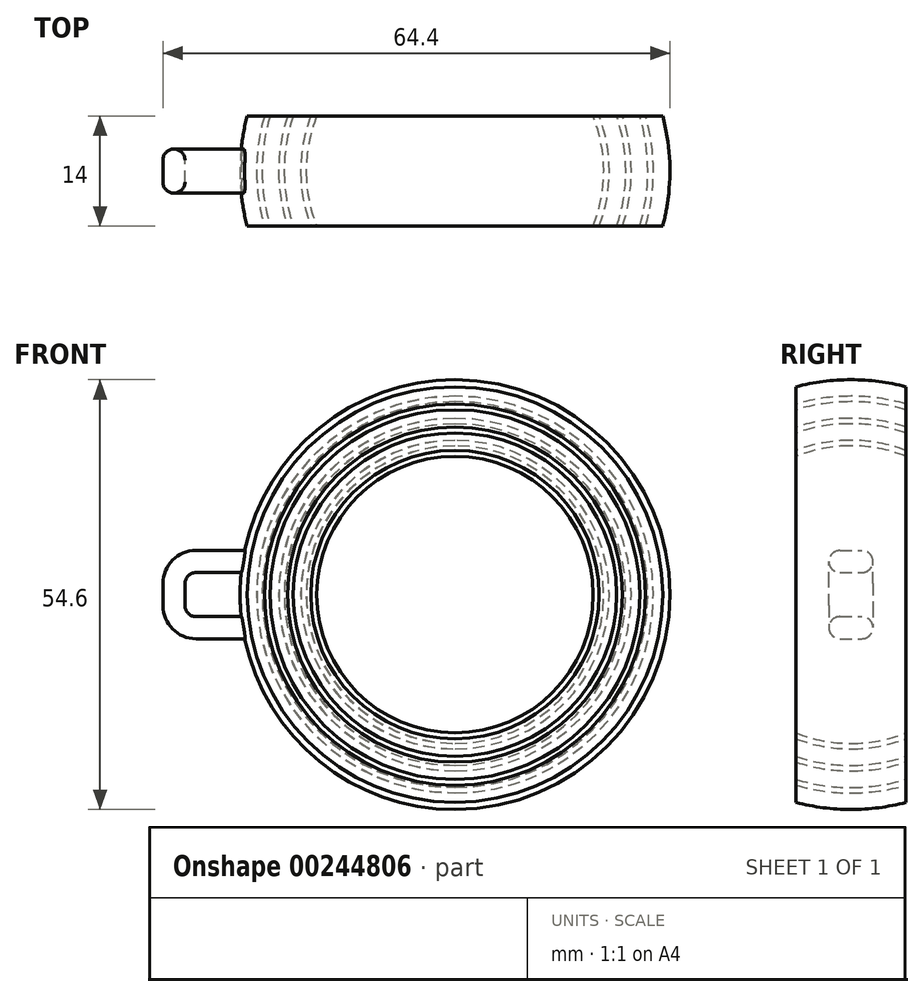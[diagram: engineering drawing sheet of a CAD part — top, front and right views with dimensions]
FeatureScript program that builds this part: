
annotation { "Feature Type Name" : "Feature", "Feature Type Description" : "" }
export const myFeature = defineFeature(function(context is Context, id is Id, definition is map)
    precondition{}
    {
        {
            var Q0;
            Q0=qCreatedBy(makeId("Front.planeOp"),FACE);
            var sketch = newSketch(context, id + "F0", { "sketchPlane" : qUnion([Q0])});
            skCircle(sketch, "E0", {"center": v(0, 0) * mm, "radius": 13.5 * mm});
            skCircle(sketch, "E1.0", {"center": v(0, 0) * mm, "radius": 14 * mm});
            skCircle(sketch, "E2.0", {"center": v(0, 0) * mm, "radius": 15.5 * mm});
            skCircle(sketch, "E3.0", {"center": v(0, 0) * mm, "radius": 16 * mm});
            skCircle(sketch, "E4.0", {"center": v(0, 0) * mm, "radius": 17.5 * mm});
            skCircle(sketch, "E5.0", {"center": v(0, 0) * mm, "radius": 18 * mm});
            skCircle(sketch, "E6.0", {"center": v(0, 0) * mm, "radius": 19.5 * mm});
            skLineSegment(sketch, "E7", {"start": v(0, 19.5) * mm, "end": v(0, -19.5) * mm});
            skSolve(sketch);
        }
        {
            var Q0;
            Q0=qCreatedBy(makeId("Top.planeOp"),FACE);
            var sketch = newSketch(context, id + "F1", { "sketchPlane" : qUnion([Q0])});
            skCircle(sketch, "E8", {"center": v(0, 0) * mm, "radius": 15 * mm});
            skSolve(sketch);
        }
        {
            var Q0;
            {var subQ0=sQuery(id+"F0.wireOp",EDGE,"E7");var subQ1=sQuery(id+"F0.wireOp",EDGE,"E0");var subQ2=makeQuery(id+"F0.imprint","INTERSECT",VERTEX,{"disambiguationData":[OD(0.0)],"derivedFrom":[subQ1,subQ0]});Q0=makeQuery(id+"F0.imprint","IMPRINT",FACE,{"disambiguationData":[TD([[makeQuery(id+"F0.imprint","IMPRINT",EDGE,{"disambiguationData":[TD([[subQ2,1.0]])],"derivedFrom":subQ1}),1.0]])]});}
            var Q1;
            {var subQ0=sQuery(id+"F0.wireOp",EDGE,"E7");var subQ1=sQuery(id+"F0.wireOp",EDGE,"E1.0");var subQ2=makeQuery(id+"F0.imprint","INTERSECT",VERTEX,{"disambiguationData":[OD(0.0)],"derivedFrom":[subQ1,subQ0]});Q1=makeQuery(id+"F0.imprint","IMPRINT",FACE,{"disambiguationData":[TD([[makeQuery(id+"F0.imprint","IMPRINT",EDGE,{"disambiguationData":[TD([[subQ2,1.0]])],"derivedFrom":subQ1}),-1.0]])]});}
            var Q2;
            {var subQ0=sQuery(id+"F0.wireOp",EDGE,"E7");var subQ1=sQuery(id+"F0.wireOp",EDGE,"E3.0");var subQ2=makeQuery(id+"F0.imprint","INTERSECT",VERTEX,{"disambiguationData":[OD(0.0)],"derivedFrom":[subQ1,subQ0]});Q2=makeQuery(id+"F0.imprint","IMPRINT",FACE,{"disambiguationData":[TD([[makeQuery(id+"F0.imprint","IMPRINT",EDGE,{"disambiguationData":[TD([[subQ2,1.0]])],"derivedFrom":subQ1}),-1.0]])]});}
            var Q3;
            {var subQ0=sQuery(id+"F0.wireOp",EDGE,"E7");var subQ1=sQuery(id+"F0.wireOp",EDGE,"E5.0");var subQ2=makeQuery(id+"F0.imprint","INTERSECT",VERTEX,{"disambiguationData":[OD(0.0)],"derivedFrom":[subQ1,subQ0]});Q3=makeQuery(id+"F0.imprint","IMPRINT",FACE,{"disambiguationData":[TD([[makeQuery(id+"F0.imprint","IMPRINT",EDGE,{"disambiguationData":[TD([[subQ2,1.0]])],"derivedFrom":subQ1}),-1.0]])]});}
            var Q4;
            Q4=sQuery(id+"F1.wireOp",EDGE,"E8");
            revolve(context, id + "F2", {"entities" : qUnion([Q0, Q1, Q2, Q3]), "axis" : qUnion([Q4]), "revolveType" : RevolveType.FULL});
        }
        {
            var Q0;
            Q0=qCreatedBy(makeId("Top.planeOp"),FACE);
            var sketch = newSketch(context, id + "F3", { "sketchPlane" : qUnion([Q0])});
            skPoint(sketch, "E9", {"position": v(0, 5) * mm});
            skPoint(sketch, "E10", {"position": v(0, -5) * mm});
            skLineSegment(sketch, "E11.bottom", {"start": v(-36.72, 5) * mm, "end": v(35.28, 5) * mm});
            skLineSegment(sketch, "E11.top", {"start": v(-36.72, 40.53) * mm, "end": v(35.28, 40.53) * mm});
            skLineSegment(sketch, "E11.left", {"start": v(-36.72, 5) * mm, "end": v(-36.72, 40.53) * mm});
            skLineSegment(sketch, "E11.right", {"start": v(35.28, 5) * mm, "end": v(35.28, 40.53) * mm});
            skLineSegment(sketch, "E12.MirrorCS", {"start": v(-36.72, -5) * mm, "end": v(-36.72, -40.53) * mm});
            skLineSegment(sketch, "E13.MirrorCS", {"start": v(-36.72, -40.53) * mm, "end": v(35.28, -40.53) * mm});
            skLineSegment(sketch, "E14.MirrorCS", {"start": v(-36.72, -5) * mm, "end": v(35.28, -5) * mm});
            skLineSegment(sketch, "E15.MirrorCS", {"start": v(35.28, -5) * mm, "end": v(35.28, -40.53) * mm});
            skSolve(sketch);
        }
        {
            var Q0;
            Q0=makeQuery(id+"F3.imprint","IMPRINT",FACE,{"disambiguationData":[TD([[makeQuery(id+"F3.imprint","IMPRINT",EDGE,{"derivedFrom":sQuery(id+"F3.wireOp",EDGE,"E11.bottom")}),1.0]])]});
            var Q1;
            Q1=makeQuery(id+"F3.imprint","IMPRINT",FACE,{"disambiguationData":[TD([[makeQuery(id+"F3.imprint","IMPRINT",EDGE,{"derivedFrom":sQuery(id+"F3.wireOp",EDGE,"E12.MirrorCS")}),1.0]])]});
            extrude(context, id + "F4", {"entities" : qUnion([Q0, Q1]), "operationType" : NewBodyOperationType.REMOVE, "oppositeDirection" : true, "depth" : 100 * mm, "hasSecondDirection" : true, "secondDirectionOppositeDirection" : false, "secondDirectionDepth" : 100 * mm});
        }
        {
            var Q0;
            Q0=qCreatedBy(makeId("Front.planeOp"),FACE);
            var sketch = newSketch(context, id + "F5", { "sketchPlane" : qUnion([Q0])});
            skLineSegment(sketch, "E16", {"start": v(-18.29, 2) * mm, "end": v(-24.5, 2) * mm});
            skLineSegment(sketch, "E17.0", {"start": v(-18.29, 4) * mm, "end": v(-26.5, 4) * mm});
            skLineSegment(sketch, "E18", {"start": v(-24.5, 2) * mm, "end": v(-24.5, 0) * mm});
            skLineSegment(sketch, "E19.0", {"start": v(-26.5, 4) * mm, "end": v(-26.5, 0) * mm});
            skLineSegment(sketch, "E20.MirrorCS", {"start": v(-26.5, -4) * mm, "end": v(-26.5, 0) * mm});
            skLineSegment(sketch, "E21.MirrorCS", {"start": v(-24.5, -2) * mm, "end": v(-24.5, 0) * mm});
            skLineSegment(sketch, "E22.MirrorCS", {"start": v(-18.29, -2) * mm, "end": v(-24.5, -2) * mm});
            skLineSegment(sketch, "E23.MirrorCS", {"start": v(-18.29, -4) * mm, "end": v(-26.5, -4) * mm});
            skLineSegment(sketch, "E24", {"start": v(-18.29, 4) * mm, "end": v(-18.29, -4) * mm});
            skSolve(sketch);
        }
        {
            var Q0;
            {var subQ4=sQuery(id+"F5.wireOp",EDGE,"E16");Q0=makeQuery(id+"F5.imprint","IMPRINT",FACE,{"disambiguationData":[TD([[makeQuery(id+"F5.imprint","IMPRINT",EDGE,{"derivedFrom":subQ4}),-1.0]])]});}
            extrude(context, id + "F6", {"entities" : qUnion([Q0]), "operationType" : NewBodyOperationType.ADD, "depth" : 2 * mm, "hasSecondDirection" : true, "secondDirectionOppositeDirection" : true, "secondDirectionDepth" : 2 * mm});
        }
        {
            var Q0;
            Q0=makeQuery(id+"F6.opExtrude","CAP_EDGE",EDGE,{"disambiguationData":[OSD([sQuery(id+"F5.wireOp",EDGE,"E17.0")])],"isStart":true});
            var Q1;
            Q1=makeQuery(id+"F6.opExtrude","CAP_EDGE",EDGE,{"disambiguationData":[OSD([sQuery(id+"F5.wireOp",EDGE,"E17.0")])],"isStart":false});
            var Q2;
            Q2=makeQuery(id+"F6.opExtrude","CAP_EDGE",EDGE,{"disambiguationData":[OSD([sQuery(id+"F5.wireOp",EDGE,"E19.0"),sQuery(id+"F5.wireOp",EDGE,"E20.MirrorCS")])],"isStart":true});
            var Q3;
            Q3=makeQuery(id+"F6.opExtrude","CAP_EDGE",EDGE,{"disambiguationData":[OSD([sQuery(id+"F5.wireOp",EDGE,"E19.0"),sQuery(id+"F5.wireOp",EDGE,"E20.MirrorCS")])],"isStart":false});
            var Q4;
            Q4=makeQuery(id+"F6.opExtrude","CAP_EDGE",EDGE,{"disambiguationData":[OSD([sQuery(id+"F5.wireOp",EDGE,"E23.MirrorCS")])],"isStart":true});
            var Q5;
            Q5=makeQuery(id+"F6.opExtrude","CAP_EDGE",EDGE,{"disambiguationData":[OSD([sQuery(id+"F5.wireOp",EDGE,"E23.MirrorCS")])],"isStart":false});
            var Q6;
            Q6=makeQuery(id+"F6.opExtrude","SWEPT_EDGE",EDGE,{"disambiguationData":[OSD([sQuery(id+"F5.wireOp",EDGE,"E16"),sQuery(id+"F5.wireOp",EDGE,"E18")])]});
            var Q7;
            Q7=makeQuery(id+"F6.opExtrude","SWEPT_EDGE",EDGE,{"disambiguationData":[OSD([sQuery(id+"F5.wireOp",EDGE,"E21.MirrorCS"),sQuery(id+"F5.wireOp",EDGE,"E22.MirrorCS")])]});
            var Q8;
            Q8=makeQuery(id+"F6.opExtrude","CAP_EDGE",EDGE,{"disambiguationData":[OSD([sQuery(id+"F5.wireOp",EDGE,"E18"),sQuery(id+"F5.wireOp",EDGE,"E21.MirrorCS")])],"isStart":true});
            var Q9;
            Q9=makeQuery(id+"F6.opExtrude","CAP_EDGE",EDGE,{"disambiguationData":[OSD([sQuery(id+"F5.wireOp",EDGE,"E22.MirrorCS")])],"isStart":true});
            var Q10;
            Q10=makeQuery(id+"F6.opExtrude","CAP_EDGE",EDGE,{"disambiguationData":[OSD([sQuery(id+"F5.wireOp",EDGE,"E16")])],"isStart":true});
            var Q11;
            Q11=makeQuery(id+"F6.opExtrude","CAP_EDGE",EDGE,{"disambiguationData":[OSD([sQuery(id+"F5.wireOp",EDGE,"E16")])],"isStart":false});
            var Q12;
            Q12=makeQuery(id+"F6.opExtrude","CAP_EDGE",EDGE,{"disambiguationData":[OSD([sQuery(id+"F5.wireOp",EDGE,"E18"),sQuery(id+"F5.wireOp",EDGE,"E21.MirrorCS")])],"isStart":false});
            var Q13;
            Q13=makeQuery(id+"F6.opExtrude","CAP_EDGE",EDGE,{"disambiguationData":[OSD([sQuery(id+"F5.wireOp",EDGE,"E22.MirrorCS")])],"isStart":false});
            fillet(context, id + "F7", {"entities" : qUnion([Q0, Q1, Q2, Q3, Q4, Q5, Q6, Q7, Q8, Q9, Q10, Q11, Q12, Q13]), "radius" : 1 * mm, "tangentPropagation" : true, "allowEdgeOverflow" : false});
        }
        {
            var Q0;
            Q0=makeQuery(id+"F6.opExtrude","SWEPT_EDGE",EDGE,{"disambiguationData":[OSD([sQuery(id+"F5.wireOp",EDGE,"E20.MirrorCS"),sQuery(id+"F5.wireOp",EDGE,"E23.MirrorCS")])]});
            var Q1;
            Q1=makeQuery(id+"F6.opExtrude","SWEPT_EDGE",EDGE,{"disambiguationData":[OSD([sQuery(id+"F5.wireOp",EDGE,"E17.0"),sQuery(id+"F5.wireOp",EDGE,"E19.0")])]});
            fillet(context, id + "F8", {"entities" : qUnion([Q0, Q1]), "radius" : 3 * mm, "tangentPropagation" : true, "allowEdgeOverflow" : false});
        }
        {
            var Q0;
            Q0=makeQuery(id+"F2.opRevolve","SWEPT_BODY",BODY,{"disambiguationData":[OSD([sQuery(id+"F0.wireOp",EDGE,"E0"),sQuery(id+"F0.wireOp",EDGE,"E7")])]});
            var Q1;
            Q1=makeQuery(id+"F2.opRevolve","SWEPT_BODY",BODY,{"disambiguationData":[OSD([sQuery(id+"F0.wireOp",EDGE,"E1.0"),sQuery(id+"F0.wireOp",EDGE,"E2.0"),sQuery(id+"F0.wireOp",EDGE,"E7")])]});
            var Q2;
            Q2=makeQuery(id+"F2.opRevolve","SWEPT_BODY",BODY,{"disambiguationData":[OSD([sQuery(id+"F0.wireOp",EDGE,"E3.0"),sQuery(id+"F0.wireOp",EDGE,"E4.0"),sQuery(id+"F0.wireOp",EDGE,"E7")])]});
            var Q3;
            Q3=makeQuery(id+"F2.opRevolve","SWEPT_BODY",BODY,{"disambiguationData":[OSD([sQuery(id+"F0.wireOp",EDGE,"E5.0"),sQuery(id+"F0.wireOp",EDGE,"E6.0"),sQuery(id+"F0.wireOp",EDGE,"E7")])]});
            var Q4;
            Q4=qCreatedBy(makeId("Origin.pointOp"),VERTEX);
            transform(context, id + "F9", {"entities" : qUnion([Q0, Q1, Q2, Q3]), "transformType" : TransformType.SCALE_UNIFORMLY, "scale" : 1.4, "scalePoint" : qUnion([Q4]), "makeCopy" : false});
        }
    });
